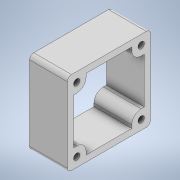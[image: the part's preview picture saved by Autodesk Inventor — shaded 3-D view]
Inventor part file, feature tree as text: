
AUTODESK INVENTOR PART (.ipt)
format: ipt  version: 2021 (Build 250183000, 183)  size: 144,384 bytes
history: native  units: mm
features: extrude x2, sketch x2, fillet x1
ambient origin geometry x8: Origin, YZ Plane, XZ Plane, XY Plane, X Axis, Y Axis, Z Axis, Center Point
bodies: Solid1 (feature_tree)
feature tree (5):
  extrude  "Extrusion1"  Depth=2.0mm
  fillet  "Fillet1"  Radius=3.05mm
  extrude  "Extrusion2"  Depth=10.0mm
  sketch  "Sketch1"  dims[d17=18.2mm d18=0.0mm d19=2.0mm d20=3.05mm]
  sketch  "Sketch2"  dims[d21=3.05mm d22=3.05mm d23=3.05mm d24=10.0mm d25=0.0mm]
